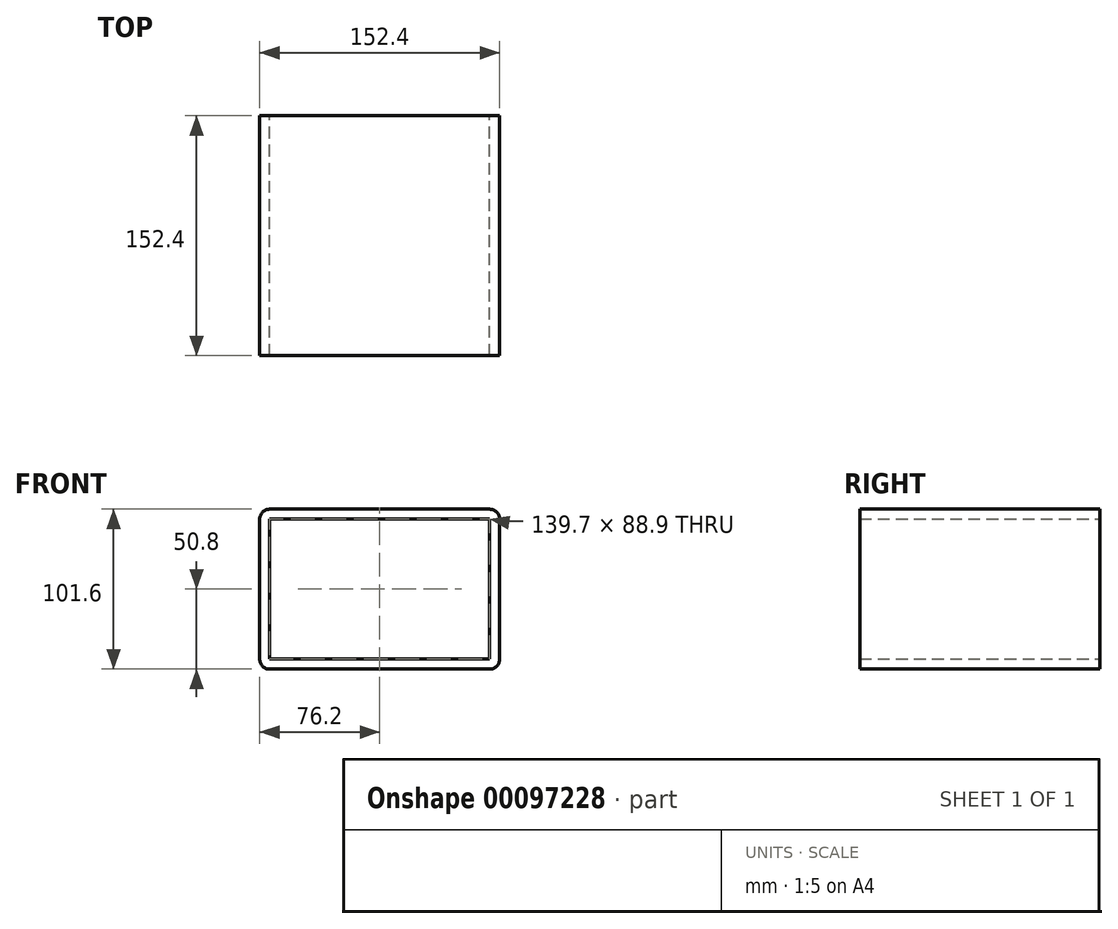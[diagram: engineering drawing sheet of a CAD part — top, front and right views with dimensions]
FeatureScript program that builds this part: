
annotation { "Feature Type Name" : "Feature", "Feature Type Description" : "" }
export const myFeature = defineFeature(function(context is Context, id is Id, definition is map)
    precondition{}
    {
        {
            var Q0;
            Q0=qCreatedBy(makeId("Front.planeOp"),FACE);
            var sketch = newSketch(context, id + "F0", { "sketchPlane" : qUnion([Q0])});
            skLineSegment(sketch, "E0.bottom", {"start": v(-69.85, 50.8) * mm, "end": v(69.85, 50.8) * mm});
            skLineSegment(sketch, "E0.top", {"start": v(-69.85, -50.8) * mm, "end": v(69.85, -50.8) * mm});
            skLineSegment(sketch, "E0.left", {"start": v(-76.2, 44.45) * mm, "end": v(-76.2, -44.45) * mm});
            skLineSegment(sketch, "E0.right", {"start": v(76.2, 44.45) * mm, "end": v(76.2, -44.45) * mm});
            skPoint(sketch, "E0.middle", {"position": v(0, 0) * mm});
            skLineSegment(sketch, "E1.0", {"start": v(-69.85, 44.45) * mm, "end": v(-69.85, -44.45) * mm});
            skLineSegment(sketch, "E1.1", {"start": v(-69.85, 44.45) * mm, "end": v(69.85, 44.45) * mm});
            skLineSegment(sketch, "E1.2", {"start": v(69.85, 44.45) * mm, "end": v(69.85, -44.45) * mm});
            skLineSegment(sketch, "E1.3", {"start": v(-69.85, -44.45) * mm, "end": v(69.85, -44.45) * mm});
            skPoint(sketch, "E2.visualSharp", {"position": v(-76.2, 50.8) * mm});
            skArc(sketch, "E2.filletArc", {"start": v(-69.85, 50.8) * mm, "mid": v(-74.34, 48.94) * mm, "end": v(-76.2, 44.45) * mm});
            skPoint(sketch, "E3.visualSharp", {"position": v(76.2, 50.8) * mm});
            skArc(sketch, "E3.filletArc", {"start": v(76.2, 44.45) * mm, "mid": v(74.34, 48.94) * mm, "end": v(69.85, 50.8) * mm});
            skPoint(sketch, "E4.visualSharp", {"position": v(76.2, -50.8) * mm});
            skArc(sketch, "E4.filletArc", {"start": v(69.85, -50.8) * mm, "mid": v(74.34, -48.94) * mm, "end": v(76.2, -44.45) * mm});
            skPoint(sketch, "E5.visualSharp", {"position": v(-76.2, -50.8) * mm});
            skArc(sketch, "E5.filletArc", {"start": v(-76.2, -44.45) * mm, "mid": v(-74.34, -48.94) * mm, "end": v(-69.85, -50.8) * mm});
            skSolve(sketch);
        }
        {
            var Q0;
            Q0=makeQuery(id+"F0.imprint","IMPRINT",FACE,{"disambiguationData":[TD([[makeQuery(id+"F0.imprint","IMPRINT",EDGE,{"derivedFrom":sQuery(id+"F0.wireOp",EDGE,"E0.bottom")}),-1.0]])]});
            extrude(context, id + "F1", {"entities" : qUnion([Q0]), "endBound" : BoundingType.SYMMETRIC, "depth" : 152.4 * mm});
        }
    });
